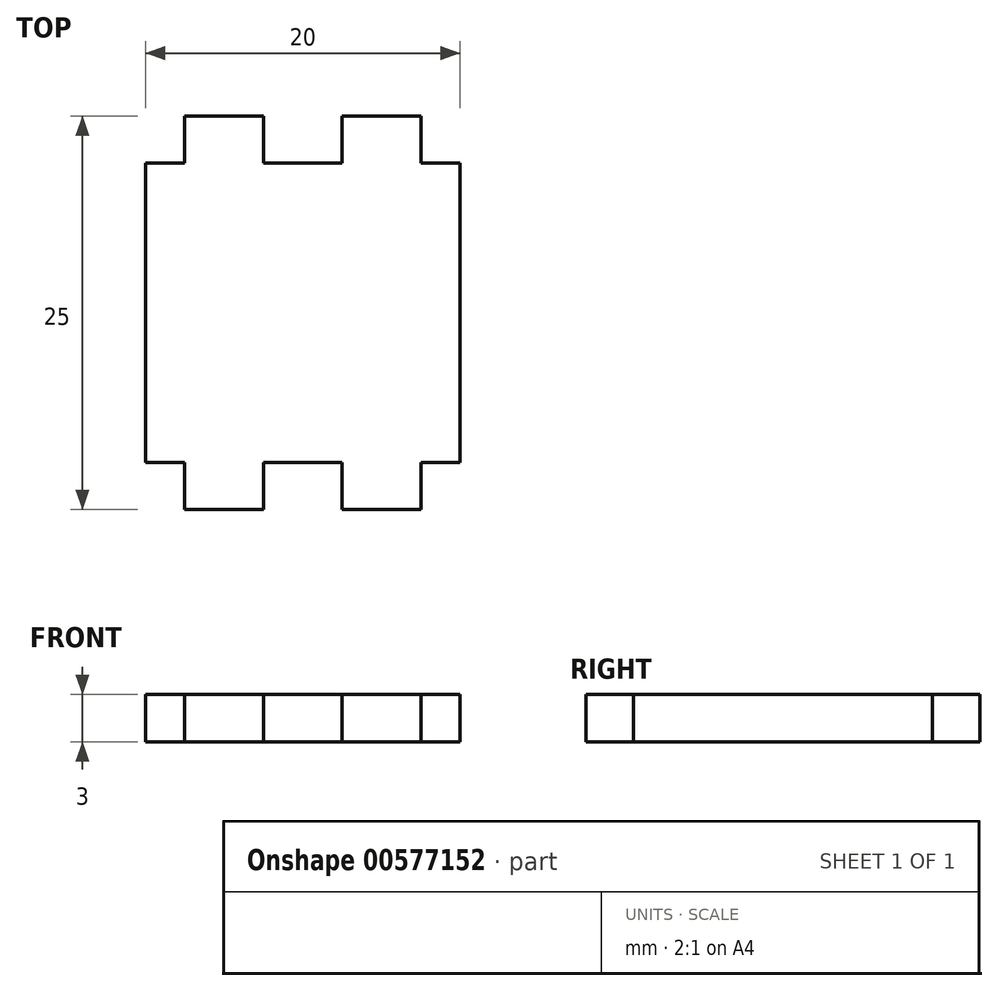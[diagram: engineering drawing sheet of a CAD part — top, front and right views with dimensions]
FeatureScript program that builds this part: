
annotation { "Feature Type Name" : "Feature", "Feature Type Description" : "" }
export const myFeature = defineFeature(function(context is Context, id is Id, definition is map)
    precondition{}
    {
        {
            var Q0;
            Q0=qCreatedBy(makeId("Top.planeOp"),FACE);
            var sketch = newSketch(context, id + "F0", { "sketchPlane" : qUnion([Q0])});
            skLineSegment(sketch, "E0", {"start": v(-10, 0) * mm, "end": v(-10, 9.5) * mm});
            skLineSegment(sketch, "E1", {"start": v(-10, 9.5) * mm, "end": v(-7.5, 9.5) * mm});
            skLineSegment(sketch, "E2", {"start": v(-7.5, 9.5) * mm, "end": v(-7.5, 12.5) * mm});
            skLineSegment(sketch, "E3", {"start": v(-7.5, 12.5) * mm, "end": v(-2.5, 12.5) * mm});
            skLineSegment(sketch, "E4", {"start": v(-2.5, 12.5) * mm, "end": v(-2.5, 9.5) * mm});
            skLineSegment(sketch, "E5", {"start": v(-2.5, 9.5) * mm, "end": v(0, 9.5) * mm});
            skLineSegment(sketch, "E6.MirrorCS", {"start": v(2.5, 9.5) * mm, "end": v(0, 9.5) * mm});
            skLineSegment(sketch, "E7.MirrorCS", {"start": v(2.5, 12.5) * mm, "end": v(2.5, 9.5) * mm});
            skLineSegment(sketch, "E8.MirrorCS", {"start": v(7.5, 12.5) * mm, "end": v(2.5, 12.5) * mm});
            skLineSegment(sketch, "E9.MirrorCS", {"start": v(7.5, 9.5) * mm, "end": v(7.5, 12.5) * mm});
            skLineSegment(sketch, "E10.MirrorCS", {"start": v(10, 9.5) * mm, "end": v(7.5, 9.5) * mm});
            skLineSegment(sketch, "E11.MirrorCS", {"start": v(10, 0) * mm, "end": v(10, 9.5) * mm});
            skLineSegment(sketch, "E12.MirrorCS", {"start": v(10, 0) * mm, "end": v(10, -9.5) * mm});
            skLineSegment(sketch, "E13.MirrorCS", {"start": v(10, -9.5) * mm, "end": v(7.5, -9.5) * mm});
            skLineSegment(sketch, "E14.MirrorCS", {"start": v(7.5, -9.5) * mm, "end": v(7.5, -12.5) * mm});
            skLineSegment(sketch, "E15.MirrorCS", {"start": v(7.5, -12.5) * mm, "end": v(2.5, -12.5) * mm});
            skLineSegment(sketch, "E16.MirrorCS", {"start": v(2.5, -12.5) * mm, "end": v(2.5, -9.5) * mm});
            skLineSegment(sketch, "E17.MirrorCS", {"start": v(2.5, -9.5) * mm, "end": v(0, -9.5) * mm});
            skLineSegment(sketch, "E18.MirrorCS", {"start": v(-2.5, -9.5) * mm, "end": v(0, -9.5) * mm});
            skLineSegment(sketch, "E19.MirrorCS", {"start": v(-2.5, -12.5) * mm, "end": v(-2.5, -9.5) * mm});
            skLineSegment(sketch, "E20.MirrorCS", {"start": v(-7.5, -12.5) * mm, "end": v(-2.5, -12.5) * mm});
            skLineSegment(sketch, "E21.MirrorCS", {"start": v(-7.5, -9.5) * mm, "end": v(-7.5, -12.5) * mm});
            skLineSegment(sketch, "E22.MirrorCS", {"start": v(-10, -9.5) * mm, "end": v(-7.5, -9.5) * mm});
            skLineSegment(sketch, "E23.MirrorCS", {"start": v(-10, 0) * mm, "end": v(-10, -9.5) * mm});
            skSolve(sketch);
        }
        {
            var Q0;
            Q0=qSketchRegion(id+"F0",true);
            extrude(context, id + "F1", {"entities" : qUnion([Q0]), "depth" : 3 * mm});
        }
    });
